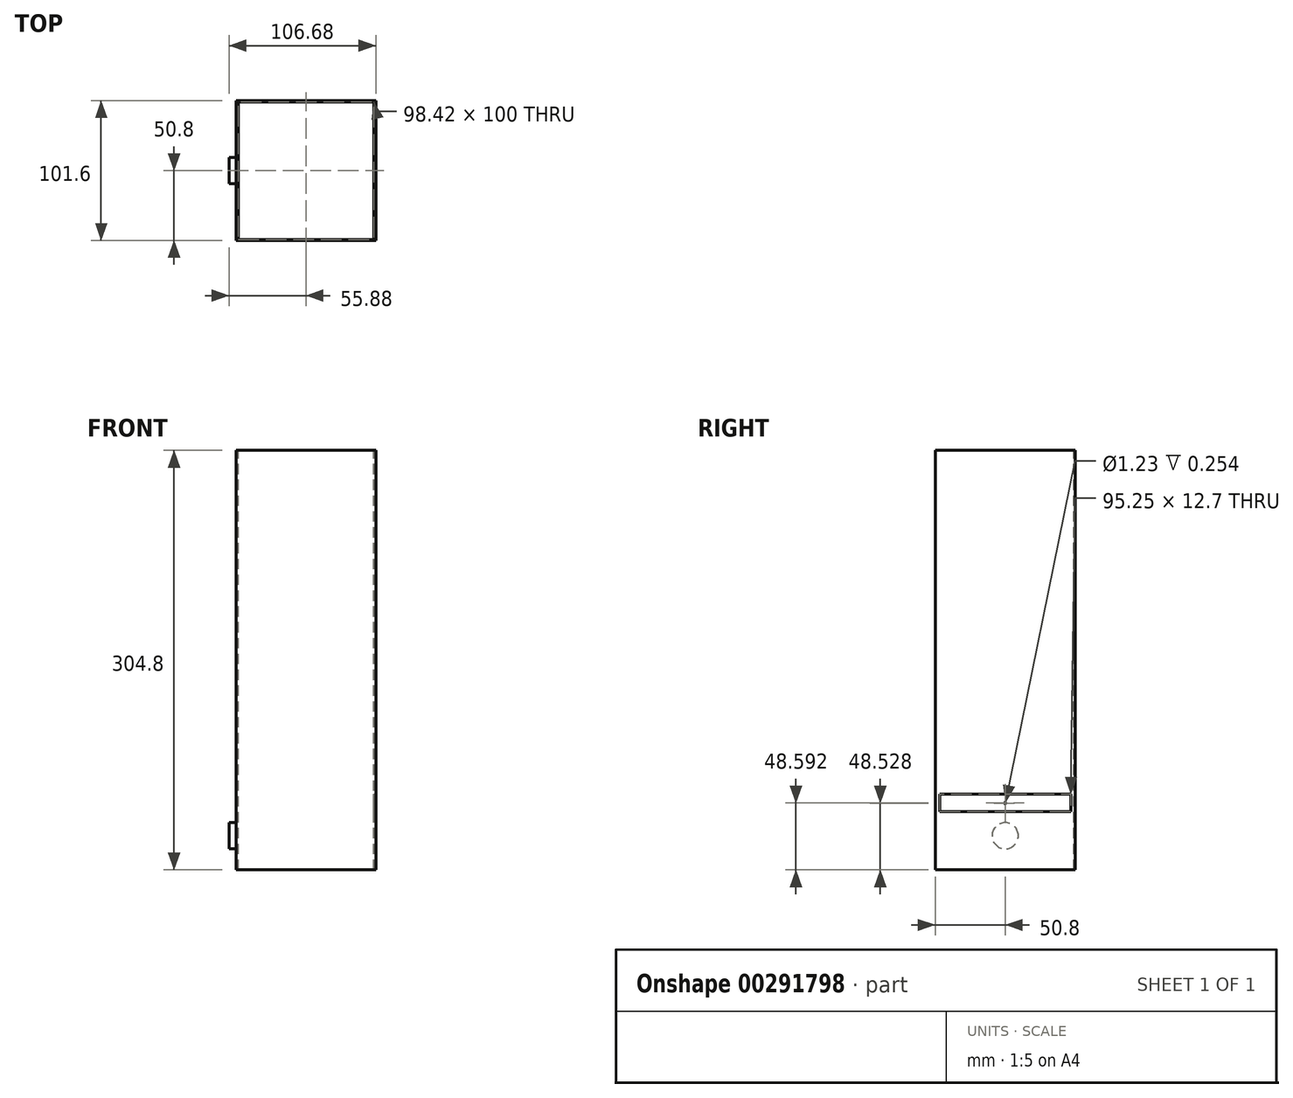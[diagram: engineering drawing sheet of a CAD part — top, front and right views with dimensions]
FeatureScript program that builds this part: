
annotation { "Feature Type Name" : "Feature", "Feature Type Description" : "" }
export const myFeature = defineFeature(function(context is Context, id is Id, definition is map)
    precondition{}
    {
        {
            var Q0;
            Q0=qCreatedBy(makeId("Front.planeOp"),FACE);
            var sketch = newSketch(context, id + "F0", { "sketchPlane" : qUnion([Q0])});
            skLineSegment(sketch, "E0.bottom", {"start": v(50.8, 152.4) * mm, "end": v(-50.8, 152.4) * mm});
            skLineSegment(sketch, "E0.top", {"start": v(50.8, -152.4) * mm, "end": v(-50.8, -152.4) * mm});
            skLineSegment(sketch, "E0.left", {"start": v(50.8, 152.4) * mm, "end": v(50.8, -152.4) * mm});
            skLineSegment(sketch, "E0.right", {"start": v(-50.8, 152.4) * mm, "end": v(-50.8, -152.4) * mm});
            skPoint(sketch, "E0.middle", {"position": v(0, 0) * mm});
            skSolve(sketch);
        }
        {
            var Q0;
            Q0 = qSketchRegion(id + "F0", true);
            extrude(context, id + "F1", {"entities" : qUnion([Q0]), "endBound" : BoundingType.SYMMETRIC, "depth" : 101.6 * mm});
        }
        {
            var Q0;
            Q0=makeQuery(id+"F1.opExtrude","SWEPT_FACE",FACE,{"disambiguationData":[OSD([sQuery(id+"F0.wireOp",EDGE,"E0.bottom")])]});
            var sketch = newSketch(context, id + "F2", { "sketchPlane" : qUnion([Q0])});
            skLineSegment(sketch, "E1.bottom", {"start": v(49.21, 50) * mm, "end": v(-49.21, 50) * mm});
            skLineSegment(sketch, "E1.top", {"start": v(49.21, -50) * mm, "end": v(-49.21, -50) * mm});
            skLineSegment(sketch, "E1.left", {"start": v(49.21, 50) * mm, "end": v(49.21, -50) * mm});
            skLineSegment(sketch, "E1.right", {"start": v(-49.21, 50) * mm, "end": v(-49.21, -50) * mm});
            skPoint(sketch, "E1.middle", {"position": v(0, 0) * mm});
            skSolve(sketch);
        }
        {
            var Q0;
            Q0 = qSketchRegion(id + "F2", true);
            extrude(context, id + "F3", {"entities" : qUnion([Q0]), "operationType" : NewBodyOperationType.REMOVE, "oppositeDirection" : true, "depth" : 304.8 * mm});
        }
        {
            var Q0;
            Q0=makeQuery(id+"F1.opExtrude","SWEPT_FACE",FACE,{"disambiguationData":[OSD([sQuery(id+"F0.wireOp",EDGE,"E0.left")])]});
            var sketch = newSketch(context, id + "F4", { "sketchPlane" : qUnion([Q0])});
            skLineSegment(sketch, "E2.bottom", {"start": v(47.63, -97.46) * mm, "end": v(-47.63, -97.46) * mm});
            skLineSegment(sketch, "E2.top", {"start": v(47.63, -110.16) * mm, "end": v(-47.63, -110.16) * mm});
            skLineSegment(sketch, "E2.left", {"start": v(47.63, -97.46) * mm, "end": v(47.63, -110.16) * mm});
            skLineSegment(sketch, "E2.right", {"start": v(-47.63, -97.46) * mm, "end": v(-47.63, -110.16) * mm});
            skPoint(sketch, "E2.middle", {"position": v(0, -103.8) * mm});
            skSolve(sketch);
        }
        {
            var Q0;
            Q0 = qSketchRegion(id + "F4", true);
            extrude(context, id + "F5", {"entities" : qUnion([Q0]), "operationType" : NewBodyOperationType.REMOVE, "oppositeDirection" : true, "depth" : 25.4 * mm});
        }
        {
            var Q0;
            Q0=makeQuery(id+"F1.opExtrude","SWEPT_FACE",FACE,{"disambiguationData":[OSD([sQuery(id+"F0.wireOp",EDGE,"E0.right")])]});
            var sketch = newSketch(context, id + "F6", { "sketchPlane" : qUnion([Q0])});
            skCircle(sketch, "E3", {"center": v(0, -127.6) * mm, "radius": 9.53 * mm});
            skSolve(sketch);
        }
        {
            var Q0;
            Q0 = qSketchRegion(id + "F6", true);
            extrude(context, id + "F7", {"entities" : qUnion([Q0]), "operationType" : NewBodyOperationType.ADD, "depth" : 5.08 * mm});
        }
        {
            var Q0;
            Q0=makeQuery(id+"F3.boolean.opBoolean","COPY",FACE,{"derivedFrom":makeQuery(id+"F3.opExtrude","SWEPT_FACE",FACE,{"disambiguationData":[OSD([sQuery(id+"F2.wireOp",EDGE,"E1.right")])]})});
            var sketch = newSketch(context, id + "F8", { "sketchPlane" : qUnion([Q0])});
            skCircle(sketch, "E4", {"center": v(0, -103.87) * mm, "radius": 0.61 * mm});
            skSolve(sketch);
        }
        {
            var Q0;
            Q0 = qSketchRegion(id + "F8", true);
            extrude(context, id + "F9", {"entities" : qUnion([Q0]), "operationType" : NewBodyOperationType.REMOVE, "oppositeDirection" : true, "depth" : 0.25 * mm});
        }
    });
